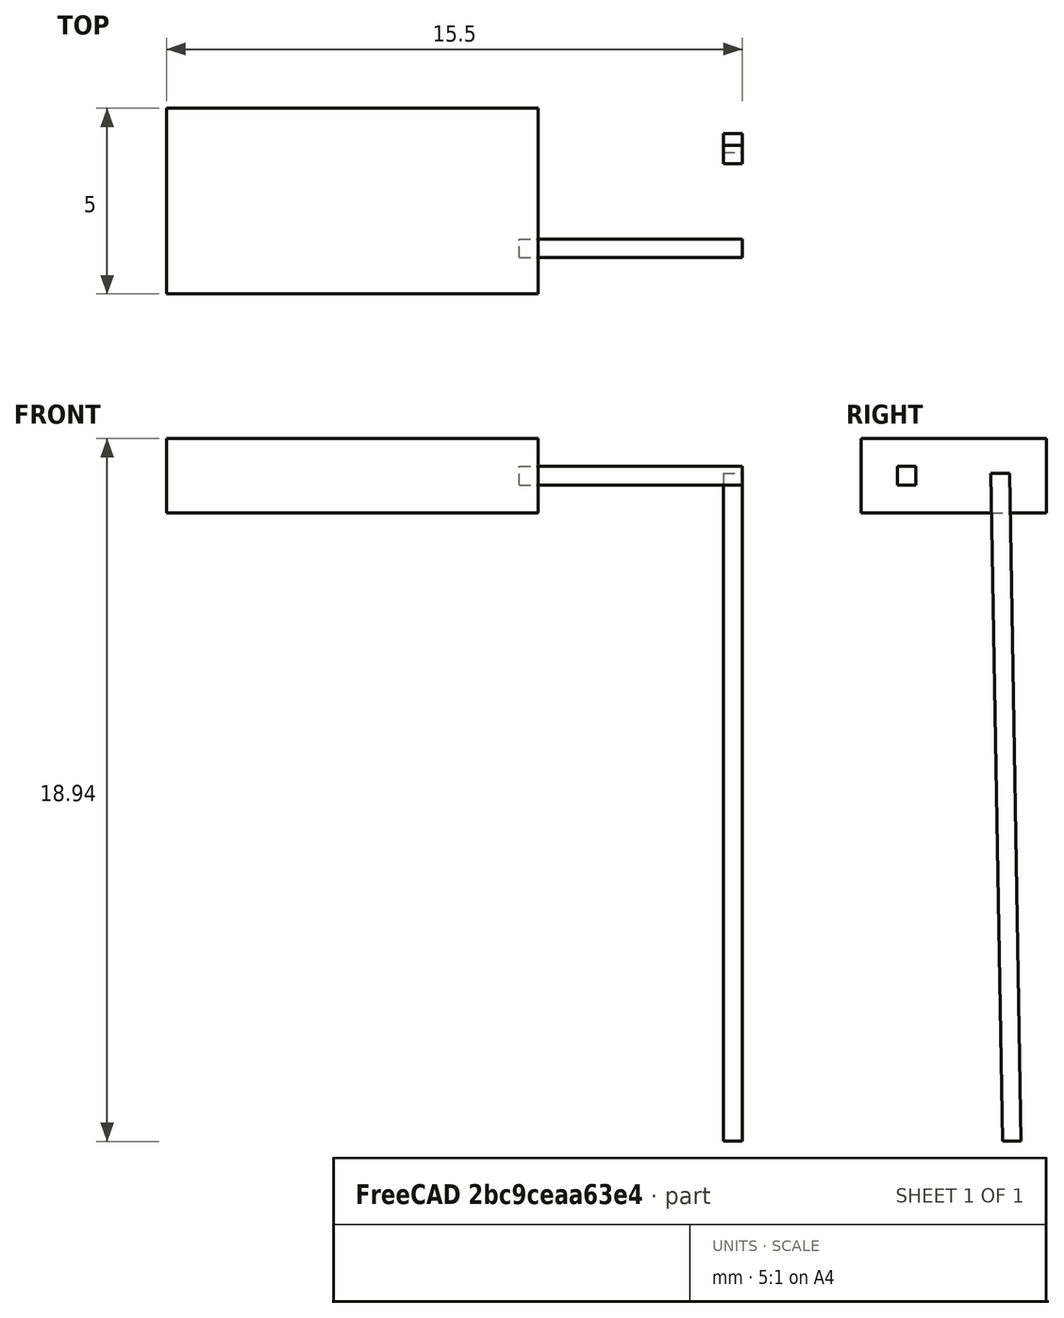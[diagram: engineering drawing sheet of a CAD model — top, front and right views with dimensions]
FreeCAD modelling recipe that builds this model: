
FCSTD DOCUMENT  (FreeCAD 0.16R)
Label: led_5x2_rj
License: All rights reserved
LicenseURL: http://en.wikipedia.org/wiki/All_rights_reserved
objects: Part::Box×3, Part::FeaturePython×2
note: 5 computed .brp shape members not serialized (recipe doc carries the construction recipe); baked Part::Feature solids carry a one-line shape summary decoded from their .brp

FEATURE [Part::Box] Box  label="Cube"
  Height = 2
  Length = 10
  Placement = pos=(-17,0,0) rot=(0,0,1;0rad)
  Width = 5
FEATURE [Part::Box] Box001  label="Cube001"
  Height = 0.5
  Length = 18
  Placement = pos=(-2,0.997303,0.982744) rot=(-0.008726,0.999924,-0.008726;1.57087rad)
  Width = 0.5
FEATURE [Part::FeaturePython] Clone  label="Clone of Cube001"  # Draft clone (typed FeaturePython)
  Objects = -> [Box001]
  Placement = pos=(-2,3.50201,1.06128) rot=(0.008726,0.999924,0.008726;1.57087rad)
  Scale = (1,1,1)
FEATURE [Part::Box] Box002  label="Cube002"
  Height = 0.5
  Length = 6
  Placement = pos=(-7.5,3.52,0.75) rot=(0,0,1;0rad)
  Width = 0.5
FEATURE [Part::FeaturePython] Clone001  label="Clone of Cube002"  # Draft clone (typed FeaturePython)
  Objects = -> [Box002]
  Placement = pos=(-7.5,0.98,0.75) rot=(0,0,1;0rad)
  Scale = (1,1,1)
